# Revit family: LR1709FG
name_source: partatom
category: Mechanical Equipment
revit_build: Autodesk Revit MEP 2016 (Build: 20150220_1215(x64)
units: mm (PartAtom-declared; Revit-internal decimal feet)

## family parameters
Cut with Voids When Loaded = No
Host = Face
OmniClass Number = 23.45.05.21.11.21
OmniClass Title = Urinals
Part Type = Normal
Room Calculation Point = No
Round Connector Dimension = Use Diameter
Shared = Yes

## types (1)
- LR1709FG
    - .125 GPF = No
    - .5 GPF = No
    1 - Off Floor, Wall Outlet = Yes
    Amperage = 0
    CW Connection = No
    Default Elevation = 9.375 "
    Description = Recessed Paper Holder
    EG - Enviro-Glaze (Interior and Exterior) Color _____________ = 0 "
    EVSFV - Master-Trol Electronic Flush Valve (N/A for Top Supply) = No
    EVSPFV - Master-Trol Electronic Flush Valve w/ Piezo Button (N/A for Top Supply) = No
    FV - Flush Valve, Mechanical (N/A for ADA) = No
    FVBO - Flush Valve by Others = No
    FVH - Flush Valve, Hydraulic (N/A for Top Supply) = No
    FVL - Flush Valve, Lever Handle (Wall Supply) = No
    HW Connection = No
    LR1709FG - High Efficiency Urinal = No
    MT - Metal Template = No
    MTPFV = No
    MTPPFV - Master-Trol PLUS Electronic Flush Valve w/ Piezo Button = No
    MVCFV - Time-Trol Electronic Flush Valve (N/A for Top Supply) = No
    Manufacturer = Acorn Engineering
    Material = Stainless Steel
    Model = 1840
    OVERALL DEPTH = 17
    OVERALL SIZE HEIGHT = 26.5
    OVERALL SIZE WIDTH = 13
    Revised Date = 07/26/16
    SW - Wall Sleeve = No
    TF - Transformer, 120VAC to 24VAC = No
    Tempered Water Connection = No
    URL = http://www.acorneng.com
    Vent Connection = No
    Voltage = 0
    W - Wall (Concealed) = Yes
    Waste Connection = Yes

## geometry (parser evidence)
native form markers: Sweep x1
no freeform markers — native parametric forms only
